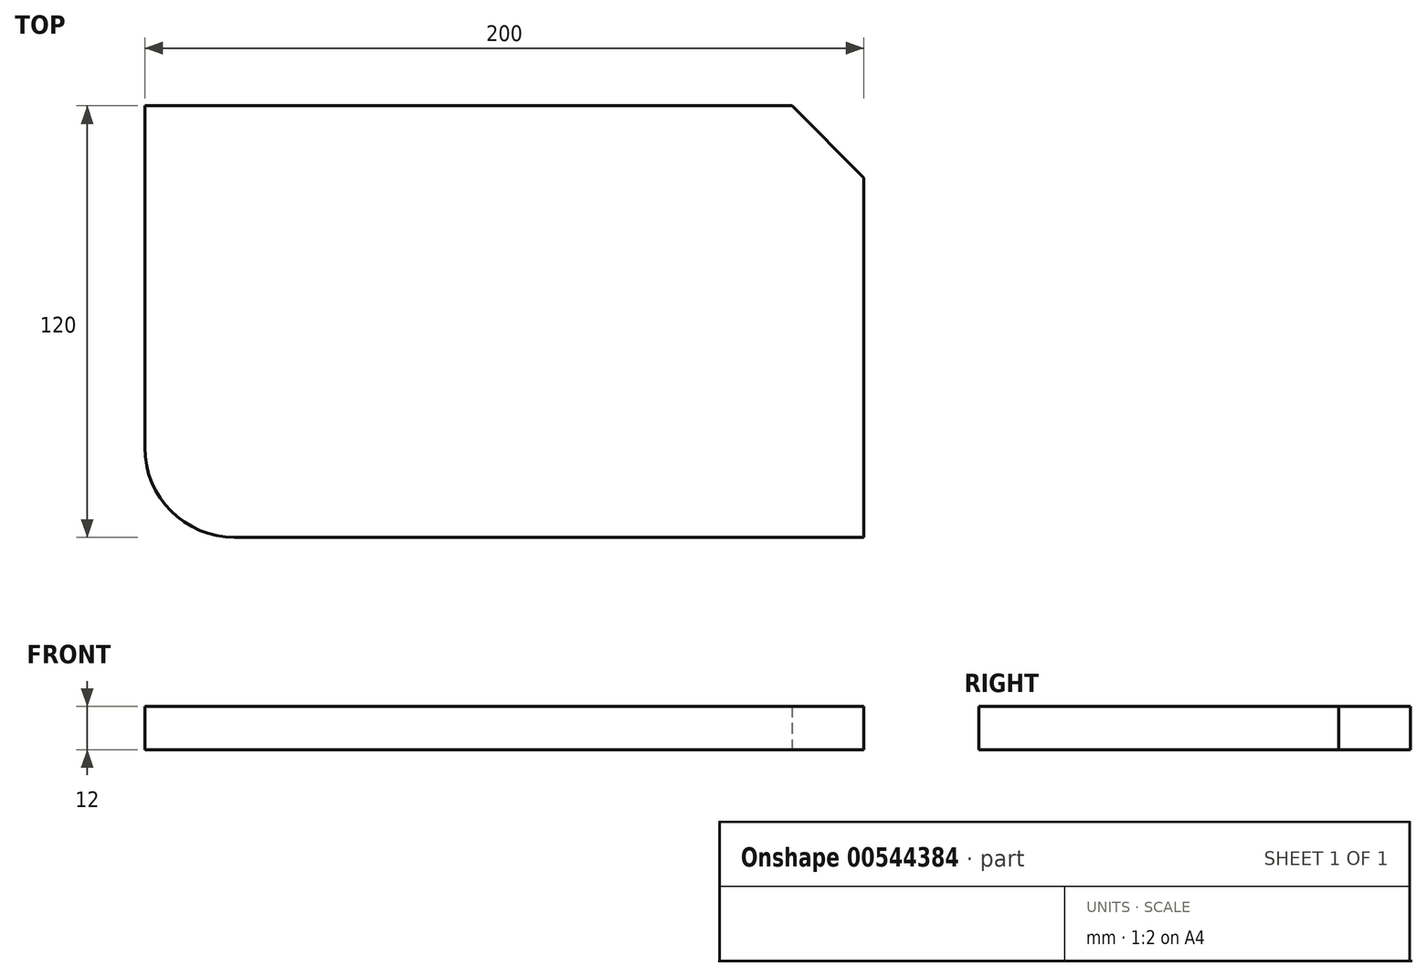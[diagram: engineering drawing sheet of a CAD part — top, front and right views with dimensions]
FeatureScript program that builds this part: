
annotation { "Feature Type Name" : "Feature", "Feature Type Description" : "" }
export const myFeature = defineFeature(function(context is Context, id is Id, definition is map)
    precondition{}
    {
        {
            var Q0;
            Q0=qCreatedBy(makeId("Top.planeOp"),FACE);
            var sketch = newSketch(context, id + "F0", { "sketchPlane" : qUnion([Q0])});
            skLineSegment(sketch, "E0.bottom", {"start": v(-200, 120) * mm, "end": v(0, 120) * mm});
            skLineSegment(sketch, "E0.top", {"start": v(-200, 0) * mm, "end": v(0, 0) * mm});
            skLineSegment(sketch, "E0.left", {"start": v(-200, 120) * mm, "end": v(-200, 0) * mm});
            skLineSegment(sketch, "E0.right", {"start": v(0, 120) * mm, "end": v(0, 0) * mm});
            skSolve(sketch);
        }
        {
            var Q0;
            Q0 = qSketchRegion(id + "F0", true);
            extrude(context, id + "F1", {"entities" : qUnion([Q0]), "depth" : 12 * mm, "offsetDistance" : 25 * mm});
        }
        {
            var Q0;
            Q0=makeQuery(id+"F1.opExtrude","SWEPT_EDGE",EDGE,{"disambiguationData":[OSD([sQuery(id+"F0.wireOp",EDGE,"E0.top"),sQuery(id+"F0.wireOp",EDGE,"E0.left")])]});
            fillet(context, id + "F2", {"entities" : qUnion([Q0]), "radius" : 25 * mm, "tangentPropagation" : true, "allowEdgeOverflow" : false});
        }
        {
            var Q0;
            Q0=makeQuery(id+"F1.opExtrude","SWEPT_EDGE",EDGE,{"disambiguationData":[OSD([sQuery(id+"F0.wireOp",EDGE,"E0.bottom"),sQuery(id+"F0.wireOp",EDGE,"E0.right")])]});
            chamfer(context, id + "F3", {"entities" : qUnion([Q0]), "width" : 20 * mm, "tangentPropagation" : true});
        }
    });
